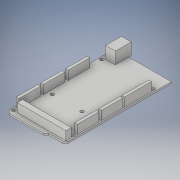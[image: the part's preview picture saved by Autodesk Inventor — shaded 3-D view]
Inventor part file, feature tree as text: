
AUTODESK INVENTOR PART (.ipt)
format: ipt  version: 2018 (Build 220112000, 112)  size: 224,256 bytes
history: native  units: in
note: dims shown in document units (in); Inventor stores cm internally (conversion verified against a paired STEP export)
features: extrude x3, sketch x3, projected_geometry x2
ambient origin geometry x8: Origin, YZ Plane, XZ Plane, XY Plane, X Axis, Y Axis, Z Axis, Center Point
bodies: Solid1 (feature_tree)
feature tree (8):
  extrude  "Extrusion1"  Depth=0.0886in
  extrude  "Extrusion2"  Depth=0.0886in
  extrude  "Extrusion3"  Depth=0.4402in
  sketch  "Sketch1"  dims[d2=0.065in d3=0.0in d4=0.0886in]
  sketch  "Sketch2"  dims[d5=45.0deg d6=0.0886in]
  projected_geometry  "Projected Loop1"
  sketch  "Sketch3"  dims[d7=45.0deg d8=0.1083in d9=1.378in d10=2.0949in d11=4.0in d12=2.0in d13=1.0474in d14=0.1in d15=0.3051in d16=3.25in d17=2.95in d18=1.9in d19=2.6024in d20=0.1252in d21=1.0965in d22=0.5748in d23=1.0in d24=0.8in d25=0.0984in d26=0.8in d27=0.1969in d28=1.8in d29=0.8in d30=0.8in d31=0.8in d32=0.3268in d33=0.0in d34=0.3598in d35=0.4402in d36=0.0in]
  projected_geometry  "Projected Loop2"
